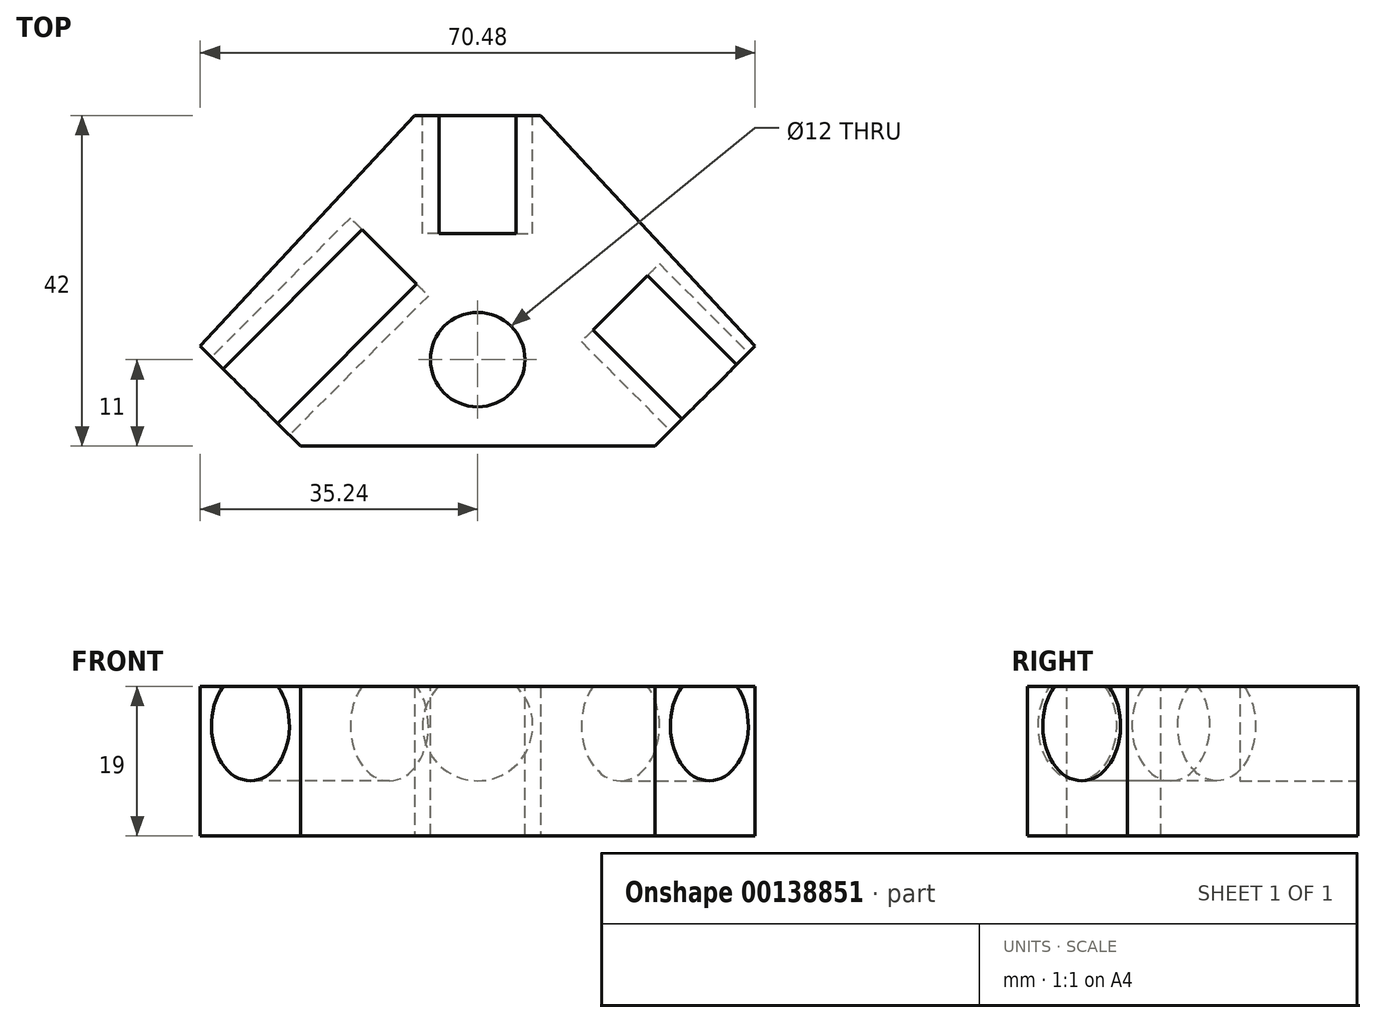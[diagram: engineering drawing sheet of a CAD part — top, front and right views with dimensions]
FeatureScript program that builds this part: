
annotation { "Feature Type Name" : "Feature", "Feature Type Description" : "" }
export const myFeature = defineFeature(function(context is Context, id is Id, definition is map)
    precondition{}
    {
        {
            var Q0;
            Q0=qCreatedBy(makeId("Top.planeOp"),FACE);
            var sketch = newSketch(context, id + "F0", { "sketchPlane" : qUnion([Q0])});
            skLineSegment(sketch, "E0", {"start": v(0, 0) * mm, "end": v(45, 0) * mm});
            skPoint(sketch, "E1.endSnap0", {"position": v(22.5, 0) * mm});
            skLineSegment(sketch, "E2", {"start": v(45, 0) * mm, "end": v(57.74, 12.71) * mm});
            skLineSegment(sketch, "E3", {"start": v(22.5, 42) * mm, "end": v(30.5, 42) * mm});
            skLineSegment(sketch, "E4", {"start": v(22.5, 42) * mm, "end": v(14.5, 42) * mm});
            skLineSegment(sketch, "E5", {"start": v(30.5, 42) * mm, "end": v(57.74, 12.71) * mm});
            skLineSegment(sketch, "E6", {"start": v(0, 0) * mm, "end": v(-12.74, 12.71) * mm});
            skLineSegment(sketch, "E7", {"start": v(-12.74, 12.71) * mm, "end": v(14.5, 42) * mm});
            skSolve(sketch);
        }
        {
            var Q0;
            Q0 = qSketchRegion(id + "F0", true);
            extrude(context, id + "F1", {"entities" : qUnion([Q0]), "depth" : 19 * mm});
        }
        {
            var Q0;
            Q0=makeQuery(id+"F1.opExtrude","SWEPT_FACE",FACE,{"disambiguationData":[OSD([sQuery(id+"F0.wireOp",EDGE,"E2")])]});
            var sketch = newSketch(context, id + "F2", { "sketchPlane" : qUnion([Q0])});
            skCircle(sketch, "E8", {"center": v(41.64, 14) * mm, "radius": 7 * mm});
            skSolve(sketch);
        }
        {
            var Q0;
            Q0 = qSketchRegion(id + "F2", true);
            extrude(context, id + "F3", {"entities" : qUnion([Q0]), "operationType" : NewBodyOperationType.REMOVE, "oppositeDirection" : true, "depth" : 16 * mm});
        }
        {
            var Q0;
            Q0=makeQuery(id+"F1.opExtrude","SWEPT_FACE",FACE,{"disambiguationData":[OSD([sQuery(id+"F0.wireOp",EDGE,"E6")])]});
            var sketch = newSketch(context, id + "F4", { "sketchPlane" : qUnion([Q0])});
            skCircle(sketch, "E9", {"center": v(-9, 14) * mm, "radius": 7 * mm});
            skPoint(sketch, "E10", {"position": v(-9, 19) * mm});
            skSolve(sketch);
        }
        {
            var Q0;
            Q0 = qSketchRegion(id + "F4", true);
            extrude(context, id + "F5", {"entities" : qUnion([Q0]), "operationType" : NewBodyOperationType.REMOVE, "oppositeDirection" : true, "depth" : 25 * mm});
        }
        {
            var Q0;
            Q0=makeQuery(id+"F1.opExtrude","SWEPT_FACE",FACE,{"disambiguationData":[OSD([sQuery(id+"F0.wireOp",EDGE,"E3"),sQuery(id+"F0.wireOp",EDGE,"E4")])]});
            var sketch = newSketch(context, id + "F6", { "sketchPlane" : qUnion([Q0])});
            skCircle(sketch, "E11", {"center": v(-22.5, 14) * mm, "radius": 7 * mm});
            skPoint(sketch, "E11.centerSnap0", {"position": v(-22.5, 19) * mm});
            skSolve(sketch);
        }
        {
            var Q0;
            Q0 = qSketchRegion(id + "F6", true);
            extrude(context, id + "F7", {"entities" : qUnion([Q0]), "operationType" : NewBodyOperationType.REMOVE, "oppositeDirection" : true, "depth" : 15 * mm});
        }
        {
            var Q0;
            Q0=makeQuery(id+"F1.opExtrude","CAP_FACE",FACE,{"disambiguationData":[OSD([sQuery(id+"F0.wireOp",EDGE,"E0"),sQuery(id+"F0.wireOp",EDGE,"E2"),sQuery(id+"F0.wireOp",EDGE,"E3"),sQuery(id+"F0.wireOp",EDGE,"E4"),sQuery(id+"F0.wireOp",EDGE,"E5"),sQuery(id+"F0.wireOp",EDGE,"E6"),sQuery(id+"F0.wireOp",EDGE,"E7")])],"isStart":false});
            var sketch = newSketch(context, id + "F8", { "sketchPlane" : qUnion([Q0])});
            skCircle(sketch, "E12", {"center": v(22.5, 11) * mm, "radius": 6 * mm});
            skPoint(sketch, "E12.centerSnap0", {"position": v(22.5, 0) * mm});
            skSolve(sketch);
        }
        {
            var Q0;
            Q0 = qSketchRegion(id + "F8", true);
            extrude(context, id + "F9", {"entities" : qUnion([Q0]), "operationType" : NewBodyOperationType.REMOVE, "endBound" : BoundingType.THROUGH_ALL, "oppositeDirection" : true, "depth" : 25 * mm});
        }
    });
